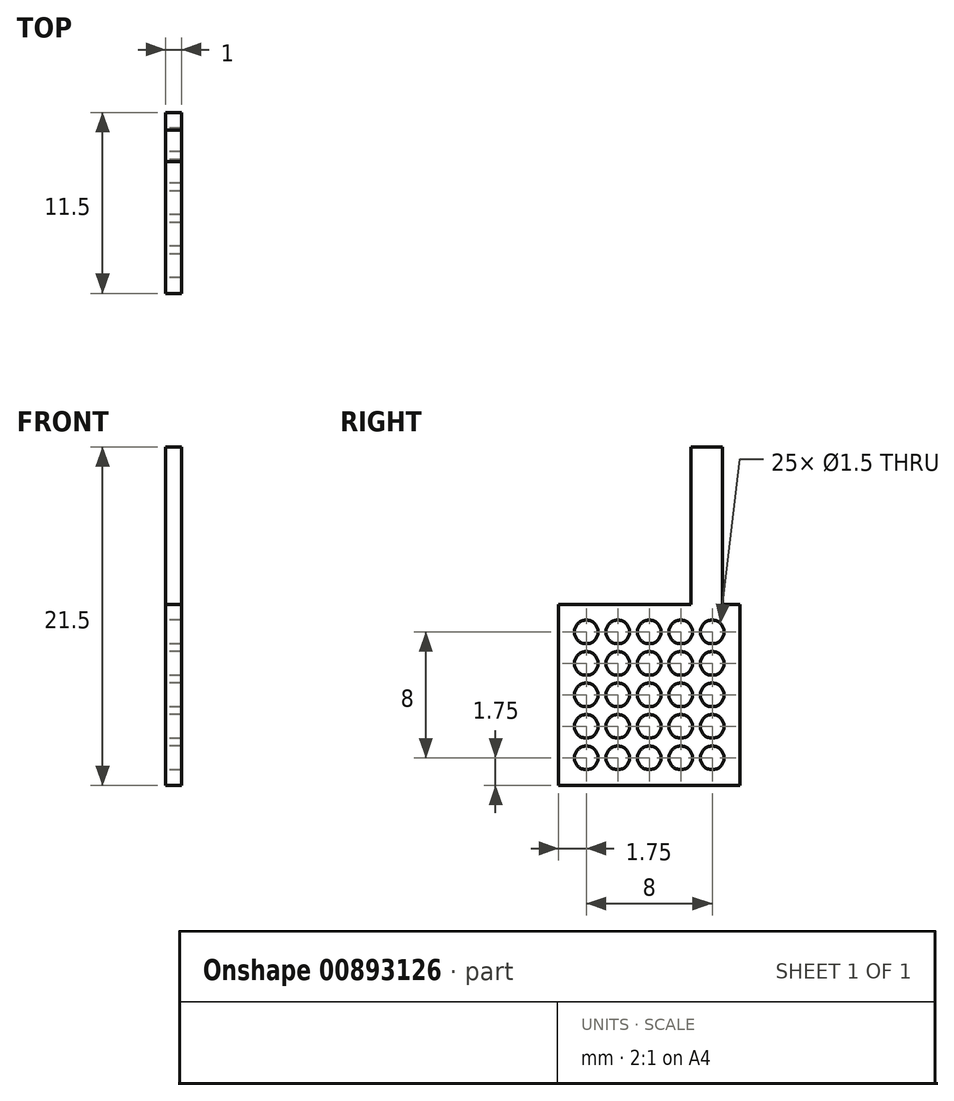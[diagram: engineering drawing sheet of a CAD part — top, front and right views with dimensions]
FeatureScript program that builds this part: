
annotation { "Feature Type Name" : "Feature", "Feature Type Description" : "" }
export const myFeature = defineFeature(function(context is Context, id is Id, definition is map)
    precondition{}
    {
        {
            var Q0;
            Q0=qCreatedBy(makeId("Right.planeOp"),FACE);
            var sketch = newSketch(context, id + "F0", { "sketchPlane" : qUnion([Q0])});
            skLineSegment(sketch, "E0.bottom", {"start": v(0, 0) * mm, "end": v(8.38, 0) * mm});
            skLineSegment(sketch, "E0.top", {"start": v(0, -11.5) * mm, "end": v(11.5, -11.5) * mm});
            skLineSegment(sketch, "E0.left", {"start": v(0, 0) * mm, "end": v(0, -11.5) * mm});
            skCircle(sketch, "E1", {"center": v(5.75, -5.75) * mm, "radius": 0.75 * mm});
            skLineSegment(sketch, "E2", {"start": v(11.5, 0) * mm, "end": v(11.5, -11.5) * mm});
            skLineSegment(sketch, "E3", {"start": v(10.38, 0) * mm, "end": v(10.38, 10) * mm});
            skLineSegment(sketch, "E4", {"start": v(10.38, 10) * mm, "end": v(8.38, 10) * mm});
            skLineSegment(sketch, "E5", {"start": v(8.38, 10) * mm, "end": v(8.38, 0) * mm});
            skLineSegment(sketch, "E6.trimOffspring", {"start": v(10.38, 0) * mm, "end": v(11.5, 0) * mm});
            skCircle(sketch, "E7", {"center": v(5.75, -3.75) * mm, "radius": 0.75 * mm});
            skCircle(sketch, "E8", {"center": v(5.75, -1.75) * mm, "radius": 0.75 * mm});
            skCircle(sketch, "E9", {"center": v(3.75, -5.75) * mm, "radius": 0.75 * mm});
            skCircle(sketch, "E10", {"center": v(1.75, -5.75) * mm, "radius": 0.75 * mm});
            skCircle(sketch, "E11.MirrorC", {"center": v(1.75, -1.75) * mm, "radius": 0.75 * mm});
            skCircle(sketch, "E12.MirrorC", {"center": v(3.75, -1.75) * mm, "radius": 0.75 * mm});
            skCircle(sketch, "E13.MirrorC", {"center": v(1.75, -3.75) * mm, "radius": 0.75 * mm});
            skCircle(sketch, "E14", {"center": v(3.75, -3.75) * mm, "radius": 0.75 * mm});
            skCircle(sketch, "E15.MirrorC", {"center": v(7.75, -1.75) * mm, "radius": 0.75 * mm});
            skCircle(sketch, "E16.MirrorC", {"center": v(9.75, -1.75) * mm, "radius": 0.75 * mm});
            skCircle(sketch, "E17.MirrorC", {"center": v(9.75, -3.75) * mm, "radius": 0.75 * mm});
            skCircle(sketch, "E18.MirrorC", {"center": v(7.75, -3.75) * mm, "radius": 0.75 * mm});
            skCircle(sketch, "E19.MirrorC", {"center": v(7.75, -5.75) * mm, "radius": 0.75 * mm});
            skCircle(sketch, "E20.MirrorC", {"center": v(9.75, -5.75) * mm, "radius": 0.75 * mm});
            skCircle(sketch, "E21.MirrorC", {"center": v(1.75, -9.75) * mm, "radius": 0.75 * mm});
            skCircle(sketch, "E22.MirrorC", {"center": v(1.75, -7.75) * mm, "radius": 0.75 * mm});
            skCircle(sketch, "E23.MirrorC", {"center": v(3.75, -7.75) * mm, "radius": 0.75 * mm});
            skCircle(sketch, "E24.MirrorC", {"center": v(3.75, -9.75) * mm, "radius": 0.75 * mm});
            skCircle(sketch, "E25.MirrorC", {"center": v(7.75, -9.75) * mm, "radius": 0.75 * mm});
            skCircle(sketch, "E26.MirrorC", {"center": v(7.75, -7.75) * mm, "radius": 0.75 * mm});
            skCircle(sketch, "E27.MirrorC", {"center": v(9.75, -9.75) * mm, "radius": 0.75 * mm});
            skCircle(sketch, "E28.MirrorC", {"center": v(9.75, -7.75) * mm, "radius": 0.75 * mm});
            skCircle(sketch, "E29.MirrorC", {"center": v(5.75, -7.75) * mm, "radius": 0.75 * mm});
            skCircle(sketch, "E30.MirrorC", {"center": v(5.75, -9.75) * mm, "radius": 0.75 * mm});
            skSolve(sketch);
        }
        {
            var Q0;
            Q0=makeQuery(id+"F0.imprint","IMPRINT",FACE,{"disambiguationData":[TD([[makeQuery(id+"F0.imprint","IMPRINT",EDGE,{"derivedFrom":sQuery(id+"F0.wireOp",EDGE,"E0.bottom")}),-1.0]])]});
            var Q1;
            Q1=makeQuery(id+"F0.imprint","IMPRINT",FACE,{"disambiguationData":[TD([[makeQuery(id+"F0.imprint","IMPRINT",EDGE,{"derivedFrom":sQuery(id+"F0.wireOp",EDGE,"r65wuaeR-pUGk-UfhY-v5oq-7bkjaNJfQmKm.bottom")}),-1.0]])]});
            var Q2;
            Q2=makeQuery(id+"F0.imprint","IMPRINT",FACE,{"disambiguationData":[TD([[makeQuery(id+"F0.imprint","IMPRINT",EDGE,{"derivedFrom":sQuery(id+"F0.wireOp",EDGE,"n5EaUuf3-CoM6-EQkv-XzT1-ydr3onYee1LO.bottom")}),1.0]])]});
            var Q3;
            Q3=makeQuery(id+"F0.imprint","IMPRINT",FACE,{"disambiguationData":[TD([[makeQuery(id+"F0.imprint","IMPRINT",EDGE,{"derivedFrom":sQuery(id+"F0.wireOp",EDGE,"2NUbogVr-x7fL-9LVX-WR3f-6RiyyzUn8nbi.bottom")}),-1.0]])]});
            extrude(context, id + "F1", {"entities" : qUnion([Q0, Q1, Q2, Q3]), "depth" : 1 * mm, "offsetDistance" : 25 * mm});
        }
    });
